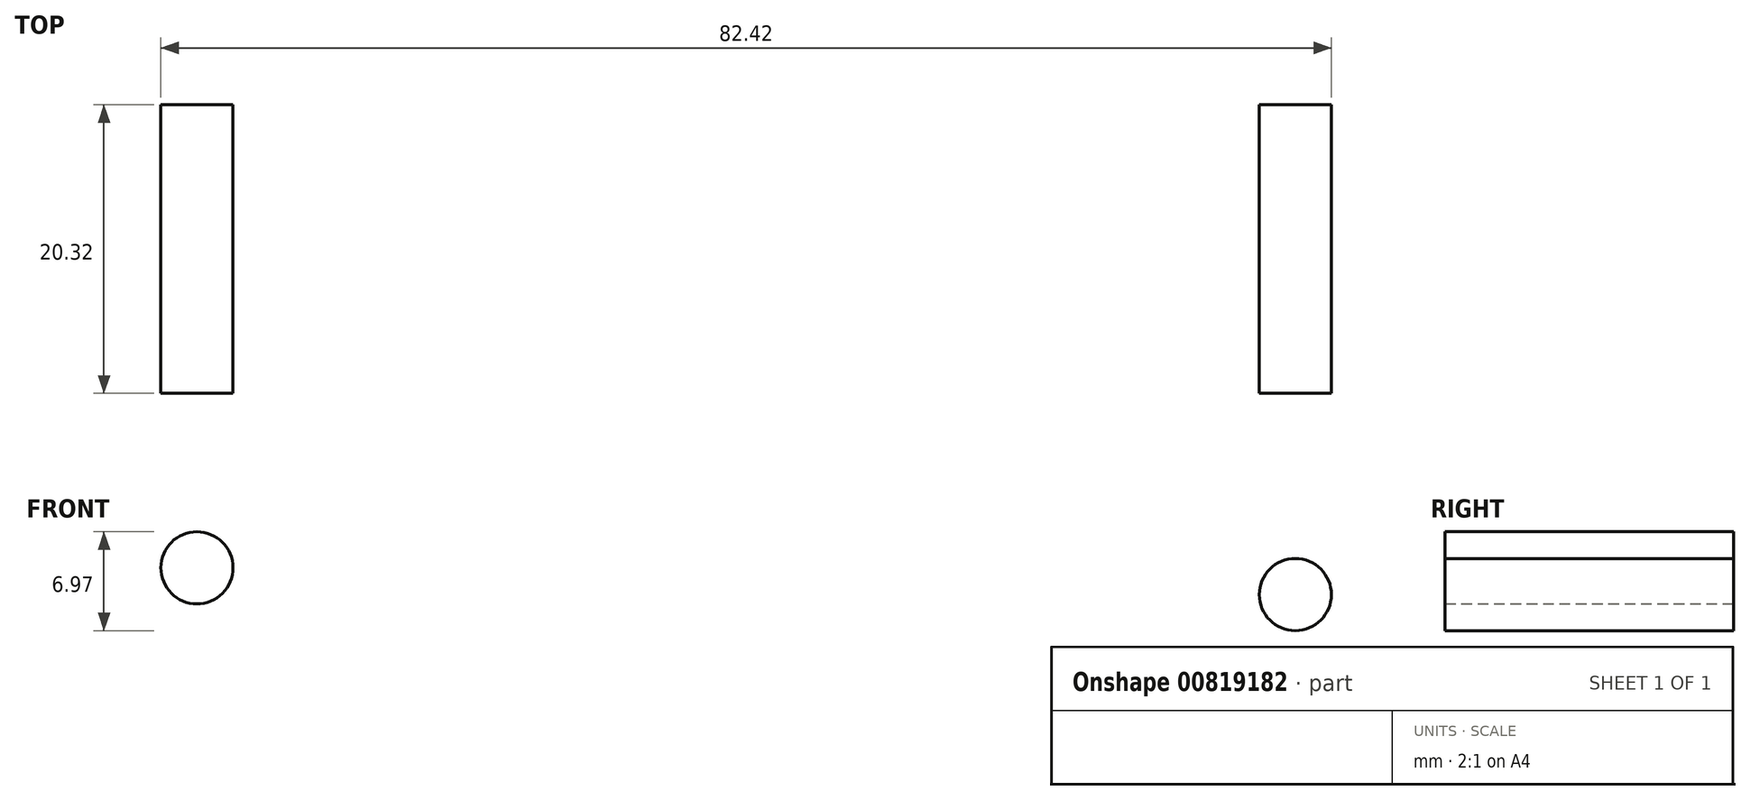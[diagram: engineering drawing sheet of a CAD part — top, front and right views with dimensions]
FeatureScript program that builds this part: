
annotation { "Feature Type Name" : "Feature", "Feature Type Description" : "" }
export const myFeature = defineFeature(function(context is Context, id is Id, definition is map)
    precondition{}
    {
        {
            var Q0;
            Q0=qCreatedBy(makeId("Front.planeOp"),FACE);
            var sketch = newSketch(context, id + "F0", { "sketchPlane" : qUnion([Q0])});
            skCircle(sketch, "E0", {"center": v(-36.31, 27.35) * mm, "radius": 2.54 * mm});
            skCircle(sketch, "E1", {"center": v(41.03, 25.46) * mm, "radius": 2.54 * mm});
            skSolve(sketch);
        }
        {
            var Q0;
            Q0 = qSketchRegion(id + "F0", true);
            extrude(context, id + "F1", {"entities" : qUnion([Q0]), "depth" : 20.32 * mm, "offsetDistance" : 25.4 * mm});
        }
    });
